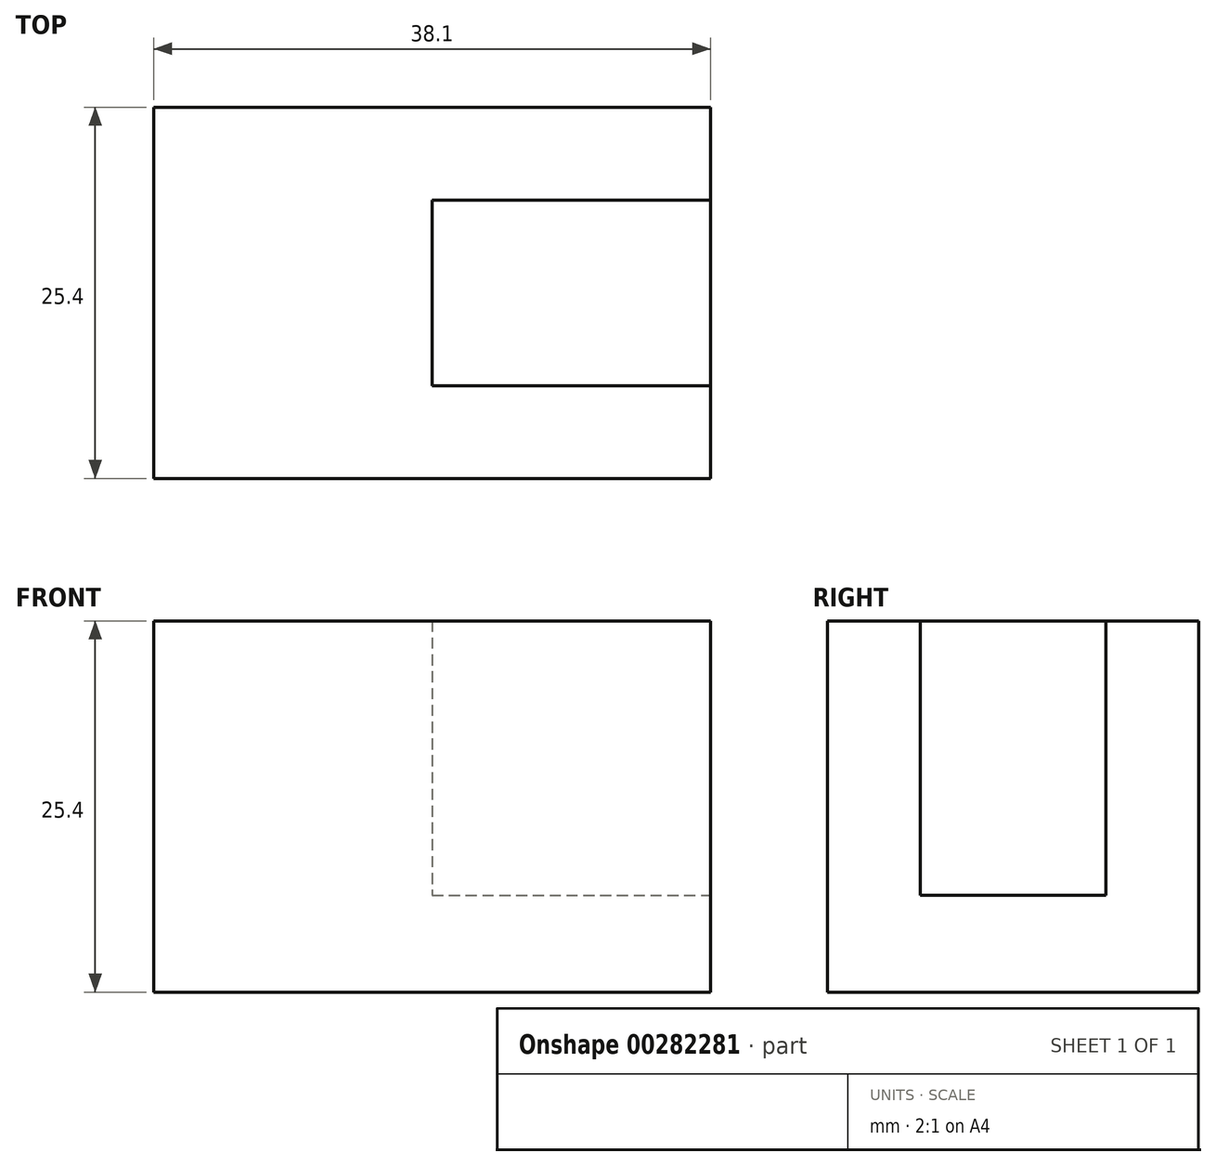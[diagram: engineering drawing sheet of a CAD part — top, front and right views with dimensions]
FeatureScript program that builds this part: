
annotation { "Feature Type Name" : "Feature", "Feature Type Description" : "" }
export const myFeature = defineFeature(function(context is Context, id is Id, definition is map)
    precondition{}
    {
        {
            var Q0;
            Q0=qCreatedBy(makeId("Top.planeOp"),FACE);
            var sketch = newSketch(context, id + "F0", { "sketchPlane" : qUnion([Q0])});
            skLineSegment(sketch, "E0", {"start": v(0, 0) * mm, "end": v(0, 25.4) * mm});
            skLineSegment(sketch, "E1", {"start": v(0, 25.4) * mm, "end": v(38.1, 25.4) * mm});
            skLineSegment(sketch, "E2", {"start": v(38.1, 0) * mm, "end": v(0, 0) * mm});
            skLineSegment(sketch, "E3", {"start": v(38.1, 25.4) * mm, "end": v(38.1, 0) * mm});
            skSolve(sketch);
        }
        {
            var Q0;
            Q0 = qSketchRegion(id + "F0", true);
            extrude(context, id + "F1", {"entities" : qUnion([Q0]), "depth" : 25.4 * mm});
        }
        {
            var Q0;
            Q0=qCreatedBy(makeId("Right.planeOp"),FACE);
            var sketch = newSketch(context, id + "F2", { "sketchPlane" : qUnion([Q0])});
            skLineSegment(sketch, "E4", {"start": v(6.35, 25.67) * mm, "end": v(6.35, 6.62) * mm});
            skLineSegment(sketch, "E5", {"start": v(6.35, 6.62) * mm, "end": v(19.05, 6.62) * mm});
            skLineSegment(sketch, "E6", {"start": v(19.05, 6.62) * mm, "end": v(19.05, 25.67) * mm});
            skLineSegment(sketch, "E7", {"start": v(19.05, 25.67) * mm, "end": v(6.35, 25.67) * mm});
            skSolve(sketch);
        }
        {
            var Q0;
            Q0 = qSketchRegion(id + "F2", true);
            extrude(context, id + "F3", {"entities" : qUnion([Q0]), "operationType" : NewBodyOperationType.REMOVE, "depth" : 19.05 * mm});
        }
        {
            var Q0;
            Q0=makeQuery(id+"F1.opExtrude","SWEPT_BODY",BODY,{"disambiguationData":[OSD([sQuery(id+"F0.wireOp",EDGE,"E0"),sQuery(id+"F0.wireOp",EDGE,"E1"),sQuery(id+"F0.wireOp",EDGE,"E2"),sQuery(id+"F0.wireOp",EDGE,"E3")])]});
            var Q1;
            Q1=makeQuery(id+"F1.opExtrude","SWEPT_EDGE",EDGE,{"disambiguationData":[OSD([sQuery(id+"F0.wireOp",EDGE,"E2"),sQuery(id+"F0.wireOp",EDGE,"E3")])]});
            transform(context, id + "F4", {"entities" : qUnion([Q0]), "transformType" : TransformType.ROTATION, "transformAxis" : qUnion([Q1]), "angle" : 180 * degree, "makeCopy" : false});
        }
    });
